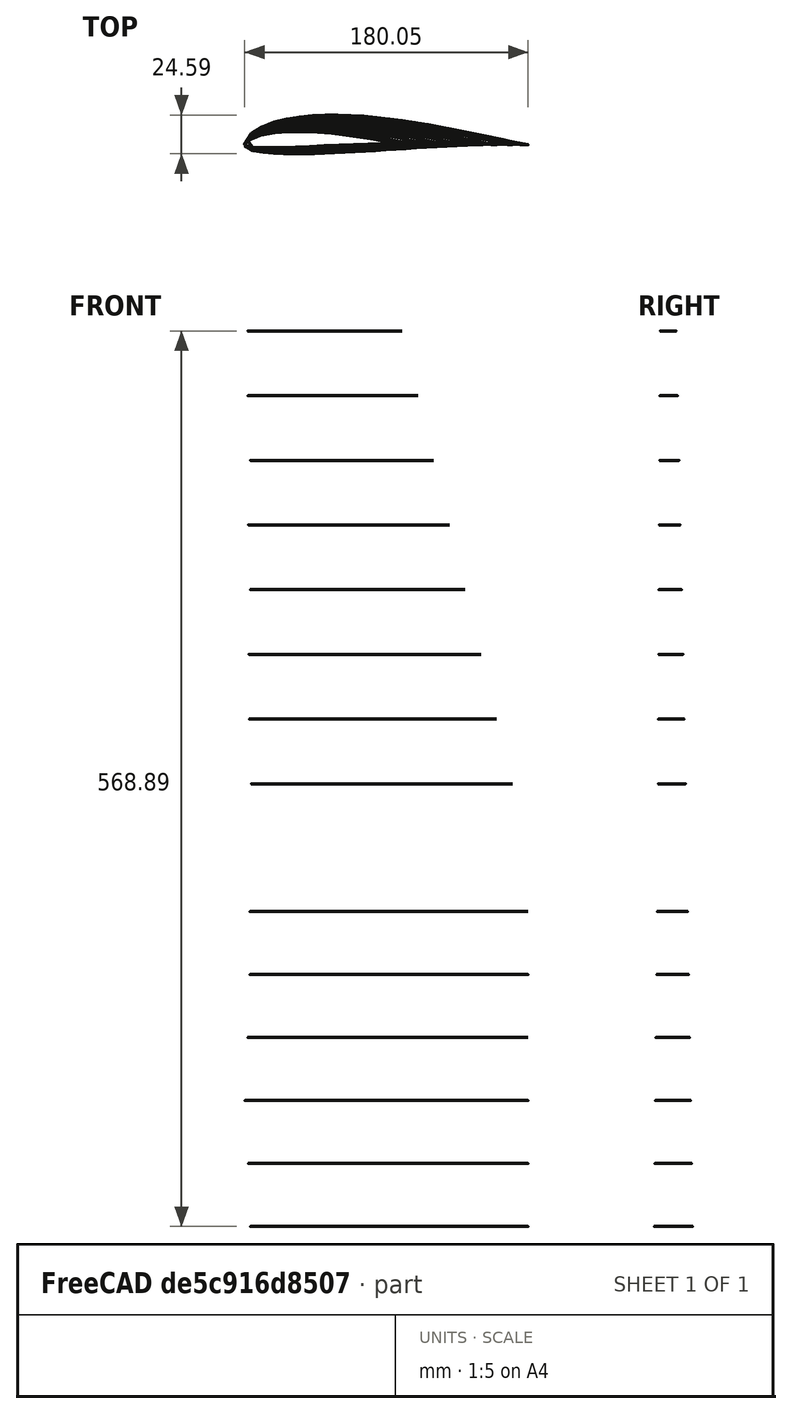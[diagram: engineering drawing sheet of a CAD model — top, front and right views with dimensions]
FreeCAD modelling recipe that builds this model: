
FCSTD DOCUMENT  (FreeCAD 0.21R33771 (Git))
Label: SD7034_wng9_drw
License: All rights reserved
LicenseURL: http://en.wikipedia.org/wiki/All_rights_reserved
objects: Part::Part2DObjectPython×23, TechDraw::DrawViewPart×15, Part::MultiCommon×14, App::DocumentObjectGroup×2, Part::Loft×2, TechDraw::DrawSVGTemplate×1, TechDraw::DrawPage×1
note: 39 computed .brp shape members not serialized (recipe doc carries the construction recipe); baked Part::Feature solids carry a one-line shape summary decoded from their .brp

FEATURE [App::DocumentObjectGroup] profile_sd7062_il  label="profile_sd7062-il"
FEATURE [Part::Part2DObjectPython] Wire  # Draft 2D object (typed FeaturePython)
  ChamferSize = 0
  Closed = true
  End = (1,0,0)
  FilletRadius = 0
  Length = 2.05949
  MakeFace = true
  Points = (61) [(1,0,0),(0.99652,0.00057,0),(0.98634,0.00242,0),(0.97004,0.00571,0),(0.94818,0.01036,0),(0.92127,0.01615,0),(0.88967,0.02289,0),(0.85381,0.03049,0),+53 more]
  Start = (1,0,0)
  Subdivisions = 0
FEATURE [Part::Part2DObjectPython] BSpline  # Draft 2D object (typed FeaturePython)
  Closed = true
  MakeFace = true
  Parameterization = 1
  Points = (60) [(1,0,0),(0.99652,0.00057,0),(0.98634,0.00242,0),(0.97004,0.00571,0),(0.94818,0.01036,0),(0.92127,0.01615,0),(0.88967,0.02289,0),(0.85381,0.03049,0),+52 more]
FEATURE [App::DocumentObjectGroup] profile_SD7032_099_88  label="profile_SD7032-099-88"
FEATURE [Part::Part2DObjectPython] Wire001  # Draft 2D object (typed FeaturePython)
  ChamferSize = 0
  Closed = true
  End = (1,0,0)
  FilletRadius = 0
  Length = 2.03505
  MakeFace = true
  Points = (61) [(1,0,0),(0.99674,0.00048,0),(0.98712,0.00204,0),(0.97155,0.00485,0),(0.95054,0.00894,0),(0.92464,0.0142,0),(0.89436,0.02041,0),(0.86021,0.02731,0),+53 more]
  Start = (1,0,0)
  Subdivisions = 0
FEATURE [Part::Part2DObjectPython] BSpline001  # Draft 2D object (typed FeaturePython)
  Closed = true
  MakeFace = true
  Parameterization = 1
  Points = (60) [(1,0,0),(0.99674,0.00048,0),(0.98712,0.00204,0),(0.97155,0.00485,0),(0.95054,0.00894,0),(0.92464,0.0142,0),(0.89436,0.02041,0),(0.86021,0.02731,0),+52 more]
FEATURE [Part::Part2DObjectPython] Clone2D  label="BSpline (2D)"  # Draft 2D object (typed FeaturePython)
  Fuse = false
  Objects = -> [BSpline]
  Scale = (180,180,1)
FEATURE [Part::Part2DObjectPython] Clone2D001  label="BSpline001 (2D)"  # Draft 2D object (typed FeaturePython)
  Fuse = false
  Objects = -> [BSpline001]
  Placement = pos=(0,0,280) rot=(0,0,1;0rad)
  Scale = (180,180,1)
FEATURE [Part::Loft] Loft
  Closed = false
  MaxDegree = 5
  Ruled = false
  Sections = -> [Clone2D,Clone2D001]
  Solid = true
FEATURE [Part::Part2DObjectPython] Clone2D002  label="BSpline001 (2D)001"  # Draft 2D object (typed FeaturePython)
  Fuse = false
  Objects = -> [BSpline001]
  Placement = pos=(0,0,280) rot=(0,0,1;0rad)
  Scale = (180,180,1)
FEATURE [Part::Part2DObjectPython] Clone2D003  label="BSpline001 (2D)002"  # Draft 2D object (typed FeaturePython)
  Fuse = false
  Objects = -> [BSpline001]
  Placement = pos=(0,0,650) rot=(0,0,1;0rad)
  Scale = (90,90,1)
FEATURE [Part::Loft] Loft001
  Closed = false
  MaxDegree = 5
  Ruled = false
  Sections = -> [Clone2D002,Clone2D003]
  Solid = true
FEATURE [Part::Part2DObjectPython] Rectangle  # Draft 2D object (typed FeaturePython)
  ChamferSize = 0
  Columns = 1
  FilletRadius = 0
  Height = 60
  Length = 220
  MakeFace = true
  Placement = pos=(-10,-15,0) rot=(0,0,1;0rad)
  Rows = 1
FEATURE [Part::Part2DObjectPython] Clone2D004  label="Rectangle (2D)"  # Draft 2D object (typed FeaturePython)
  Fuse = false
  Objects = -> [Rectangle]
  Placement = pos=(-15,-20,40) rot=(0,0,1;0rad)
  Scale = (1,1,1)
FEATURE [Part::MultiCommon] Common
  Shapes = -> [Clone2D004,Loft]
FEATURE [Part::Part2DObjectPython] Clone2D005  label="Rectangle (2D)001"  # Draft 2D object (typed FeaturePython)
  Fuse = false
  Objects = -> [Rectangle]
  Placement = pos=(-15,-20,80) rot=(0,0,1;0rad)
  Scale = (1,1,1)
FEATURE [Part::MultiCommon] Common001
  Shapes = -> [Clone2D005,Loft]
FEATURE [Part::Part2DObjectPython] Clone2D006  label="Rectangle (2D)002"  # Draft 2D object (typed FeaturePython)
  Fuse = false
  Objects = -> [Rectangle]
  Placement = pos=(-15,-20,120) rot=(0,0,1;0rad)
  Scale = (1,1,1)
FEATURE [Part::MultiCommon] Common002
  Shapes = -> [Clone2D006,Loft]
FEATURE [Part::Part2DObjectPython] Clone2D007  label="Rectangle (2D)003"  # Draft 2D object (typed FeaturePython)
  Fuse = false
  Objects = -> [Rectangle]
  Placement = pos=(-15,-20,160) rot=(0,0,1;0rad)
  Scale = (1,1,1)
FEATURE [Part::MultiCommon] Common003
  Shapes = -> [Clone2D007,Loft]
FEATURE [Part::Part2DObjectPython] Clone2D008  label="Rectangle (2D)004"  # Draft 2D object (typed FeaturePython)
  Fuse = false
  Objects = -> [Rectangle]
  Placement = pos=(-15,-20,200) rot=(0,0,1;0rad)
  Scale = (1,1,1)
FEATURE [Part::MultiCommon] Common004
  Shapes = -> [Clone2D008,Loft]
FEATURE [Part::Part2DObjectPython] Clone2D009  label="Rectangle (2D)005"  # Draft 2D object (typed FeaturePython)
  Fuse = false
  Objects = -> [Rectangle]
  Placement = pos=(-15,-20,240) rot=(0,0,1;0rad)
  Scale = (1,1,1)
FEATURE [Part::MultiCommon] Common005
  Shapes = -> [Clone2D009,Loft]
FEATURE [Part::Part2DObjectPython] Clone2D010  label="Rectangle (2D)006"  # Draft 2D object (typed FeaturePython)
  Fuse = false
  Objects = -> [Rectangle]
  Placement = pos=(-15,-20,321.111) rot=(0,0,1;0rad)
  Scale = (1,1,1)
FEATURE [Part::MultiCommon] Common006
  Shapes = -> [Clone2D010,Loft001]
FEATURE [Part::Part2DObjectPython] Clone2D011  label="Rectangle (2D)007"  # Draft 2D object (typed FeaturePython)
  Fuse = false
  Objects = -> [Rectangle]
  Placement = pos=(-15,-20,362.222) rot=(0,0,1;0rad)
  Scale = (1,1,1)
FEATURE [Part::MultiCommon] Common007
  Shapes = -> [Clone2D011,Loft001]
FEATURE [Part::Part2DObjectPython] Clone2D012  label="Rectangle (2D)008"  # Draft 2D object (typed FeaturePython)
  Fuse = false
  Objects = -> [Rectangle]
  Placement = pos=(-15,-20,403.333) rot=(0,0,1;0rad)
  Scale = (1,1,1)
FEATURE [Part::MultiCommon] Common008
  Shapes = -> [Clone2D012,Loft001]
FEATURE [Part::Part2DObjectPython] Clone2D013  label="Rectangle (2D)009"  # Draft 2D object (typed FeaturePython)
  Fuse = false
  Objects = -> [Rectangle]
  Placement = pos=(-15,-20,444.444) rot=(0,0,1;0rad)
  Scale = (1,1,1)
FEATURE [Part::MultiCommon] Common009
  Shapes = -> [Clone2D013,Loft001]
FEATURE [Part::Part2DObjectPython] Clone2D014  label="Rectangle (2D)010"  # Draft 2D object (typed FeaturePython)
  Fuse = false
  Objects = -> [Rectangle]
  Placement = pos=(-15,-20,485.556) rot=(0,0,1;0rad)
  Scale = (1,1,1)
FEATURE [Part::MultiCommon] Common010
  Shapes = -> [Clone2D014,Loft001]
FEATURE [Part::Part2DObjectPython] Clone2D015  label="Rectangle (2D)011"  # Draft 2D object (typed FeaturePython)
  Fuse = false
  Objects = -> [Rectangle]
  Placement = pos=(-15,-20,526.667) rot=(0,0,1;0rad)
  Scale = (1,1,1)
FEATURE [Part::MultiCommon] Common011
  Shapes = -> [Clone2D015,Loft001]
FEATURE [Part::Part2DObjectPython] Clone2D016  label="Rectangle (2D)012"  # Draft 2D object (typed FeaturePython)
  Fuse = false
  Objects = -> [Rectangle]
  Placement = pos=(-15,-20,567.778) rot=(0,0,1;0rad)
  Scale = (1,1,1)
FEATURE [Part::MultiCommon] Common012
  Shapes = -> [Clone2D016,Loft001]
FEATURE [Part::Part2DObjectPython] Clone2D017  label="Rectangle (2D)013"  # Draft 2D object (typed FeaturePython)
  Fuse = false
  Objects = -> [Rectangle]
  Placement = pos=(-15,-20,608.889) rot=(0,0,1;0rad)
  Scale = (1,1,1)
FEATURE [Part::MultiCommon] Common013
  Shapes = -> [Clone2D017,Loft001]
FEATURE [TechDraw::DrawSVGTemplate] Template
  Height = 420
  Orientation = 1
  Template = <path>
  Width = 594
FEATURE [TechDraw::DrawViewPart] View
  CoarseView = false
  Direction = (-0.67,0.52,0.55)
  Focus = 100
  HardHidden = false
  IsoCount = 0
  IsoHidden = false
  IsoVisible = false
  LockPosition = false
  Perspective = false
  Rotation = 0
  ScaleType = 0
  ScrubCount = 0
  SeamHidden = false
  SeamVisible = false
  SmoothHidden = false
  SmoothVisible = true
  Source = -> [Common013]
  X = 50
  XDirection = (0,0.15,0.15)
  Y = 380
FEATURE [TechDraw::DrawViewPart] View001
  CoarseView = false
  Direction = (-0.67,0.52,0.55)
  Focus = 100
  HardHidden = false
  IsoCount = 0
  IsoHidden = false
  IsoVisible = false
  LockPosition = false
  Perspective = false
  Rotation = 0
  ScaleType = 0
  ScrubCount = 0
  SeamHidden = false
  SeamVisible = false
  SmoothHidden = false
  SmoothVisible = true
  Source = -> [Common012]
  X = 53.5
  XDirection = (0,0.15,0.15)
  Y = 360
FEATURE [TechDraw::DrawViewPart] View002
  CoarseView = false
  Direction = (-0.67,0.52,0.55)
  Focus = 100
  HardHidden = false
  IsoCount = 0
  IsoHidden = false
  IsoVisible = false
  LockPosition = false
  Perspective = false
  Rotation = 0
  ScaleType = 0
  ScrubCount = 0
  SeamHidden = false
  SeamVisible = false
  SmoothHidden = false
  SmoothVisible = true
  Source = -> [Common011]
  X = 57
  XDirection = (0,0.15,0.15)
  Y = 340
FEATURE [TechDraw::DrawViewPart] View003
  CoarseView = false
  Direction = (-0.67,0.52,0.55)
  Focus = 100
  HardHidden = false
  IsoCount = 0
  IsoHidden = false
  IsoVisible = false
  LockPosition = false
  Perspective = false
  Rotation = 0
  ScaleType = 0
  ScrubCount = 0
  SeamHidden = false
  SeamVisible = false
  SmoothHidden = false
  SmoothVisible = true
  Source = -> [Common010]
  X = 60.5
  XDirection = (0,0.15,0.15)
  Y = 320
FEATURE [TechDraw::DrawViewPart] View004
  CoarseView = false
  Direction = (-0.67,0.52,0.55)
  Focus = 100
  HardHidden = false
  IsoCount = 0
  IsoHidden = false
  IsoVisible = false
  LockPosition = false
  Perspective = false
  Rotation = 0
  ScaleType = 0
  ScrubCount = 0
  SeamHidden = false
  SeamVisible = false
  SmoothHidden = false
  SmoothVisible = true
  Source = -> [Common009]
  X = 64
  XDirection = (0,0.15,0.15)
  Y = 300
FEATURE [TechDraw::DrawViewPart] View005
  CoarseView = false
  Direction = (-0.67,0.52,0.55)
  Focus = 100
  HardHidden = false
  IsoCount = 0
  IsoHidden = false
  IsoVisible = false
  LockPosition = false
  Perspective = false
  Rotation = 0
  ScaleType = 0
  ScrubCount = 0
  SeamHidden = false
  SeamVisible = false
  SmoothHidden = false
  SmoothVisible = true
  Source = -> [Common008]
  X = 67.5
  XDirection = (0,0.15,0.15)
  Y = 280
FEATURE [TechDraw::DrawViewPart] View006
  CoarseView = false
  Direction = (-0.67,0.52,0.55)
  Focus = 100
  HardHidden = false
  IsoCount = 0
  IsoHidden = false
  IsoVisible = false
  LockPosition = false
  Perspective = false
  Rotation = 0
  ScaleType = 0
  ScrubCount = 0
  SeamHidden = false
  SeamVisible = false
  SmoothHidden = false
  SmoothVisible = true
  Source = -> [Common007]
  X = 71
  XDirection = (0,0.15,0.15)
  Y = 260
FEATURE [TechDraw::DrawViewPart] View007
  CoarseView = false
  Direction = (-0.67,0.52,0.55)
  Focus = 100
  HardHidden = false
  IsoCount = 0
  IsoHidden = false
  IsoVisible = false
  LockPosition = false
  Perspective = false
  Rotation = 0
  ScaleType = 0
  ScrubCount = 0
  SeamHidden = false
  SeamVisible = false
  SmoothHidden = false
  SmoothVisible = true
  Source = -> [Common006]
  X = 74.5
  XDirection = (0,0.15,0.15)
  Y = 240
FEATURE [TechDraw::DrawViewPart] View008
  CoarseView = false
  Direction = (-0.67,0.52,0.55)
  Focus = 100
  HardHidden = false
  IsoCount = 0
  IsoHidden = false
  IsoVisible = false
  LockPosition = false
  Perspective = false
  Rotation = 0
  ScaleType = 0
  ScrubCount = 0
  SeamHidden = false
  SeamVisible = false
  SmoothHidden = false
  SmoothVisible = true
  Source = -> [Clone2D001]
  X = 78
  XDirection = (0,0.15,0.15)
  Y = 220
FEATURE [TechDraw::DrawViewPart] View009
  CoarseView = false
  Direction = (-0.67,0.52,0.55)
  Focus = 100
  HardHidden = false
  IsoCount = 0
  IsoHidden = false
  IsoVisible = false
  LockPosition = false
  Perspective = false
  Rotation = 0
  ScaleType = 0
  ScrubCount = 0
  SeamHidden = false
  SeamVisible = false
  SmoothHidden = false
  SmoothVisible = true
  Source = -> [Common005]
  X = 81.5
  XDirection = (0,0.15,0.15)
  Y = 200
FEATURE [TechDraw::DrawViewPart] View010
  CoarseView = false
  Direction = (-0.67,0.52,0.55)
  Focus = 100
  HardHidden = false
  IsoCount = 0
  IsoHidden = false
  IsoVisible = false
  LockPosition = false
  Perspective = false
  Rotation = 0
  ScaleType = 0
  ScrubCount = 0
  SeamHidden = false
  SeamVisible = false
  SmoothHidden = false
  SmoothVisible = true
  Source = -> [Common004]
  X = 200
  XDirection = (0,0.15,0.15)
  Y = 380
FEATURE [TechDraw::DrawViewPart] View011
  CoarseView = false
  Direction = (-0.67,0.52,0.55)
  Focus = 100
  HardHidden = false
  IsoCount = 0
  IsoHidden = false
  IsoVisible = false
  LockPosition = false
  Perspective = false
  Rotation = 0
  ScaleType = 0
  ScrubCount = 0
  SeamHidden = false
  SeamVisible = false
  SmoothHidden = false
  SmoothVisible = true
  Source = -> [Common003]
  X = 200
  XDirection = (0,0.15,0.15)
  Y = 360
FEATURE [TechDraw::DrawViewPart] View012
  CoarseView = false
  Direction = (-0.67,0.52,0.55)
  Focus = 100
  HardHidden = false
  IsoCount = 0
  IsoHidden = false
  IsoVisible = false
  LockPosition = false
  Perspective = false
  Rotation = 0
  ScaleType = 0
  ScrubCount = 0
  SeamHidden = false
  SeamVisible = false
  SmoothHidden = false
  SmoothVisible = true
  Source = -> [Common002]
  X = 200
  XDirection = (0,0.15,0.15)
  Y = 340
FEATURE [TechDraw::DrawViewPart] View013
  CoarseView = false
  Direction = (-0.67,0.52,0.55)
  Focus = 100
  HardHidden = false
  IsoCount = 0
  IsoHidden = false
  IsoVisible = false
  LockPosition = false
  Perspective = false
  Rotation = 0
  ScaleType = 0
  ScrubCount = 0
  SeamHidden = false
  SeamVisible = false
  SmoothHidden = false
  SmoothVisible = true
  Source = -> [Common001]
  X = 200
  XDirection = (0,0.15,0.15)
  Y = 320
FEATURE [TechDraw::DrawViewPart] View014
  CoarseView = false
  Direction = (-0.67,0.52,0.55)
  Focus = 100
  HardHidden = false
  IsoCount = 0
  IsoHidden = false
  IsoVisible = false
  LockPosition = false
  Perspective = false
  Rotation = 0
  ScaleType = 0
  ScrubCount = 0
  SeamHidden = false
  SeamVisible = false
  SmoothHidden = false
  SmoothVisible = true
  Source = -> [Common]
  X = 200
  XDirection = (0,0.15,0.15)
  Y = 300
FEATURE [TechDraw::DrawPage] Page
  KeepUpdated = true
  NextBalloonIndex = 1
  ProjectionType = 0
  Template = -> Template
  Views = -> [View,View001,View002,View003,View004,View005,View006,View007,View008,View009,View010,View011,View012,View013,View014]
note: 1 file-system path scrubbed to <path> (originals preserved in the JSON sidecar)
